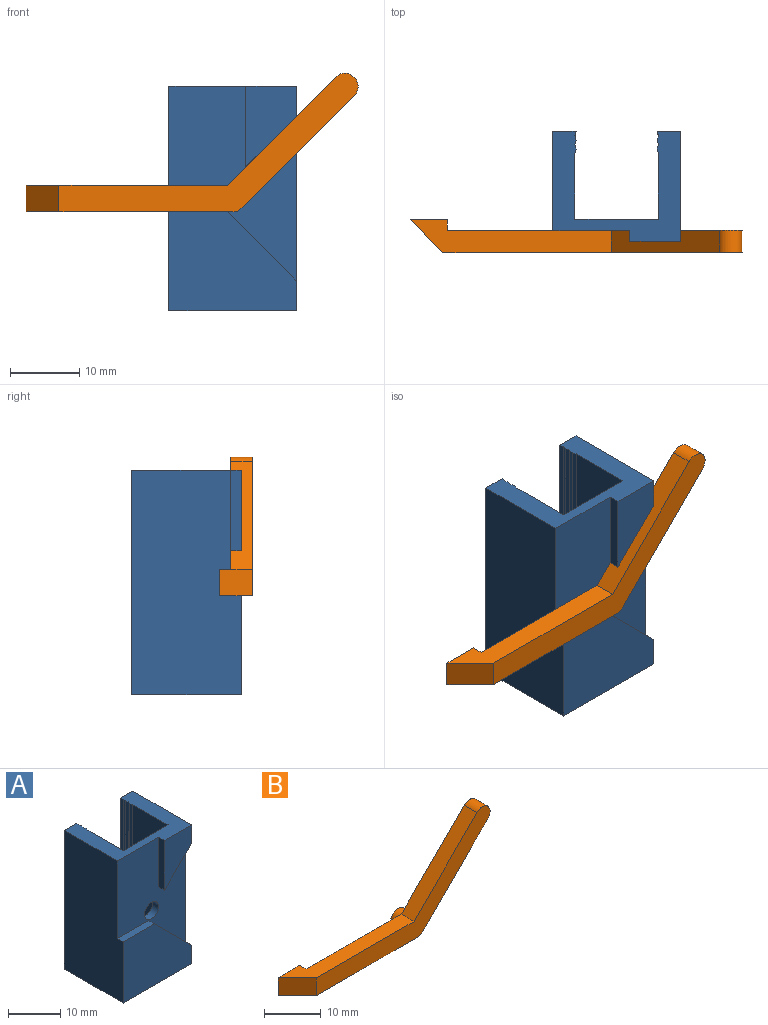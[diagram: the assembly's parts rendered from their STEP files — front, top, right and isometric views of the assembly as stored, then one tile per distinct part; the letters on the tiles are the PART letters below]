
ASSEMBLY  parts=2 mates=1
PART A: 27 faces, bbox 18.4x15.9x32.4 mm
  f0: plane 28.09x18.42mm, normal (0,-1,0), area 313.8mm2, adj f1,f2,f3,f20,f21,f23,f24,f25
  f1: plane 18.42x15.88mm, normal (0,0,1), area 122mm2, adj f0,f2,f3,f4,f5,f6,f7,f8
  f2: plane 32.39x15.88mm, normal (-1,0,0), area 485.4mm2, adj f0,f1,f16,f18,f25,f26
  f3: plane 32.39x15.88mm, normal (1,0,0), area 476.3mm2, adj f0,f1,f4,f16,f22,f23,f24,f26
  f4: plane 32.39x3.33mm, normal (0,1,0), area 108mm2, adj f1,f3,f5,f16
  f5: plane 32.39x0.64mm, normal (-0.97,-0.24,0), area 21.2mm2, adj f1,f4,f6,f16
  f6: plane 32.39x0.64mm, normal (-0.97,0.24,0), area 21.2mm2, adj f1,f5,f7,f16
  f7: plane 32.39x0.64mm, normal (-0.97,-0.24,0), area 21.2mm2, adj f1,f6,f8,f16
  f8: plane 32.39x0.64mm, normal (-0.97,0.24,0), area 21.2mm2, adj f1,f7,f9,f16
  f9: plane 32.39x0.64mm, normal (-0.97,-0.24,0), area 21.2mm2, adj f1,f8,f10,f16
  f10: plane 32.39x9.53mm, normal (-1,0,0), area 308.5mm2, adj f1,f9,f11,f16
  f11: plane 32.39x12.07mm, normal (0,1,0), area 379.3mm2, adj f1,f10,f12,f16,f20
  f12: plane 32.39x9.53mm, normal (1,0,0), area 308.5mm2, adj f1,f11,f13,f16
  f13: plane 32.39x0.64mm, normal (0.97,-0.24,0), area 21.2mm2, adj f1,f12,f14,f16
  f14: plane 32.39x0.64mm, normal (0.97,0.24,0), area 21.2mm2, adj f1,f13,f15,f16
  f15: plane 32.39x0.64mm, normal (0.97,-0.24,0), area 21.2mm2, adj f1,f14,f16,f17
  f16: plane 18.42x15.88mm, normal (0,0,-1), area 139.6mm2, adj f2,f3,f4,f5,f6,f7,f8,f9
  f17: plane 32.39x0.64mm, normal (0.97,0.24,0), area 21.2mm2, adj f1,f15,f16,f19
  f18: plane 32.39x3.33mm, normal (0,1,0), area 108mm2, adj f1,f2,f16,f19
  f19: plane 32.39x0.64mm, normal (0.97,-0.24,0), area 21.2mm2, adj f1,f16,f17,f18
  f20: cylinder r=1.91mm len=3.81mm, axis (0,1,0), area 19mm2, adj f0,f11
  f21: plane 11.59x1.59mm, normal (-1,0,0), area 18.4mm2, adj f0,f1,f22,f23
  f22: plane 11.59x7.3mm, normal (0,-1,0), area 58mm2, adj f1,f3,f21,f23
  f23: plane 7.3x7.3mm, normal (0.71,0,-0.71), area 16.4mm2, adj f0,f3,f21,f22
  f24: plane 10x10mm, normal (0.71,0,0.71), area 22.4mm2, adj f0,f3,f25,f26
  f25: plane 8.42x1.59mm, normal (0,0,1), area 13.4mm2, adj f0,f2,f24,f26
  f26: plane 18.42x14.29mm, normal (0,-1,0), area 213.1mm2, adj f2,f3,f16,f24,f25
PART B: 12 faces, bbox 47.9x4.8x20 mm
  f0: plane 43.18x20mm, normal (0,-1,0), area 188.4mm2, adj f2,f3,f4,f5,f6,f7,f11
  f1: plane 42.55x20mm, normal (0,1,0), area 174.6mm2, adj f2,f3,f4,f5,f6,f7,f10
  f2: cylinder r=1.91mm len=4.76mm, axis (0,1,0), area 23.8mm2, adj f0,f1,f3,f7,f8
  f3: plane 16.19x16.19mm, normal (0.71,0,-0.71), area 72.7mm2, adj f0,f1,f2,f4
  f4: cylinder r=1.91mm len=3.25mm, axis (0,1,0), area 19mm2, adj f0,f1,f3,f5
  f5: plane 15.63x15.63mm, normal (-0.71,0,0.71), area 70.2mm2, adj f0,f1,f4,f6
  f6: plane 29.06x4.76mm, normal (0,0,1), area 89.5mm2, adj f0,f1,f5,f9,f10,f11
  f7: plane 29.85x4.76mm, normal (0,0,-1), area 92mm2, adj f0,f1,f2,f9,f10,f11
  f8: plane 3.81x3.81mm, normal (0,1,0), area 11.4mm2, adj f2
  f9: plane 5.4x3.81mm, normal (0,1,0), area 20.6mm2, adj f6,f7,f10,f11
  f10: plane 3.81x1.59mm, normal (1,0,0), area 6mm2, adj f1,f6,f7,f9
  f11: plane 4.76x4.76mm, normal (-0.71,-0.71,0), area 25.7mm2, adj f0,f6,f7,f9
PLACE A t=(-10.89,5.56,2.56)mm fixed
PLACE B t=(-10.89,5.56,2.56)mm
MATE revolute B.f2 <-> A.f20  axis (0,1,0) through (4.35,5.56,2.56)mm
